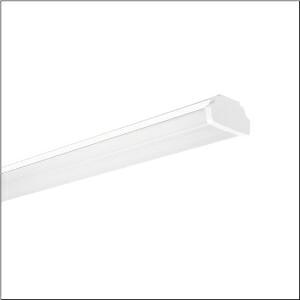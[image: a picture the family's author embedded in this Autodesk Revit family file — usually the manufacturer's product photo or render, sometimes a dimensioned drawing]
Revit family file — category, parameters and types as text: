
# Revit family: modario_r__31_ho_53bm812c1v4105_deab
name_source: partatom
category: Lighting Fixtures
units: mm (PartAtom-declared; Revit-internal decimal feet)

## family parameters
Cut with Voids When Loaded = No
Host = Face
Light Source = No
Part Type = Normal
Room Calculation Point = No
Round Connector Dimension = Use Diameter
Shared = No

## types (1)
- --- (1 x LED, 10520 lm, 63.8 W, 4000K)
    Apparent Load = 64 VA
    CIE Flux Codes = 47 80 95 92 100
    Color Rendering = 80
    Color Temperature = 4000K
    Default Elevation = 1800 mm
    Description = Modario® 31 HO, luminaire insert, of sheet steel, coil coated, white, length: 1.495mm, width: 81mm, height: 82mm, 5x system unit, system units: 299mm, LED rated luminous flux: 10.520lm, light colour: 840, control gear: ON/OFF Multilumen, CLOi, control gear: ECG Multilumen, with plug, 3-pole, with phase selection, mains connection: 220..240V, AC, 50/60Hz, start of lifetime: 64W, end of service life: 73W, through-wiring accessed according to module size, primary optical cover: cover, of PMMA, light emission: direct distribution, primary light characteristic: symmetric, protection rating (complete): IP20, protection rating (LED compartment): IP50, insulation class (complete): insulation class I (protective earthing), certification: CE, ENEC, VDE, UKCA, impact resistance: IK03, permissible ambient temperature for indoor applications: -35..+35°C, corresponds to IFS (International Featured Standards) requirements for safety and quality in the food industry, reducing of maximum allowable ambient temperature of 5°C with ceiling mounting, packaging unit: 1 piece
    Height = 92 mm
    Lamp = 1 x LED
    Lamp Light Flux = 10520 lm
    Lamp Power = 63.8 W
    Lamp count = 1
    Length = 1495 mm
    Luminous efficacy = 165 lm/W
    Manufacturer = Siteco
    ModVariant = No
    Model = 53BM812C1V4105
    Mounting Place = Ceiling
    Mounting Type = Pendant
    Number of Poles = 1
    OnlyDefault = Yes
    Power Factor = 1
    Product Name = Modario® 31 HO
    Product group = luminaire insert
    ProductGroupID = 901
    Protection Class = Protection class I
    Protection Degree = IP 20
    RLX_Detail_Level = 1
    RLX_Emergency_Light_Flux = 0 lm
    RLX_Emergency_Type = 0
    RLX_Emergency_Type_DB = No
    RlxData = <blob elided: 40077 chars, md5=2361e6e3>
    Socket = socket
    Standby Power = 0 W
    System Light Flux = 10520 lm
    System Power = 64 W
    Type Comments = factory setting: luminous flux: 100 % | (A | C | E) | 144 mA
    Type Image = l_1300283.jpg
    URL = http://relux.com
    VarID = @adj_154955
    Voltage = 0 V
    Weight = 0.00 kg
    Width = 81 mm

## geometry (parser evidence)
native form markers: Blend x4, Sweep x12
no freeform markers — native parametric forms only
